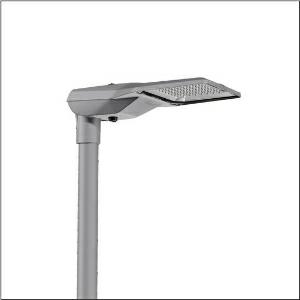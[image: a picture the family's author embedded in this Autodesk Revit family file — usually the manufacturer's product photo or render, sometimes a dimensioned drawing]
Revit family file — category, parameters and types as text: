
# Revit family: streetlight_sl_21_iq_midi___pc-r_5xe3g31y08mb_65a2
name_source: partatom
category: Lighting Fixtures
units: mm (PartAtom-declared; Revit-internal decimal feet)

## family parameters
Cut with Voids When Loaded = No
Host = Face
Light Source = No
Part Type = Normal
Room Calculation Point = No
Round Connector Dimension = Use Diameter
Shared = No

## types (1)
- --- (1 x LED, 17070 lm, 129.3 W, 3000K)
    Apparent Load = 129 VA
    CIE Flux Codes = 38 78 98 100 100
    Color Rendering = 70
    Color Temperature = 3000K
    Default Elevation = 1800 mm
    Description = Streetlight SL 21 iQ midi, mast luminaire, primary light control with lens, of PMMA, primary optical cover: cover, of toughened safety glass, transparent, light distribution: PC-R, light emission: direct distribution, primary light characteristic: asymmetric, right, installation type: post-top, side-entry, LED, High Power LED, rated luminous flux: 17.070lm, luminous efficacy: 132lm/W, light colour: 730, colour temperature: 3000K, control gear: iQ-Street Remote, D4i with power reduction, control: pre-setting: logarithmic dimming characteristic, Street-Remote, Auto-Match, Temp-Guard, Lumen-Switch, Night-Set, Smart-Wire, Light-Fading, Desk-Remote (wireless, voltage-free reading and setting of iQ features in the workshop via application-optimized NFC function/RFID function), optimised constant luminous flux control (CLO 2.0), mains connection: 230..240V, AC, 50/60Hz, start of lifetime: 129W, end of service life: 142W, reduction: 56W, luminaire housing, of diecast aluminium, powder-coated, Siteco® metallic grey (DB 702S), corrosivity category C5 mid according to DIN EN ISO 12944, please order mast flange separately, inclination adjustable: 0°, 5°, 10°, 15°, sealing non-destructively replaceable, multi-level sealing system, length: 644mm, width: 335mm, height: 110mm, mast flange for spigot size: 42mm (side-entry): 5XC10008XM4, 60/48mm (side-entry/post-top): 5XC10108XM2, 76/60mm (side-entry/post-top): 5XC10108XM1, mounting height: 4..8m, Smart Interface below and above, protection rating (complete): IP66, insulation class (complete): insulation class II (safety insulation), certification: CE, ENEC, ENEC+, VDE, impact resistance: IK10, permissible operating ambient temperature for outdoor applications: -40..+50°C, standard-compliant lighting for roads and squares, packaging unit: 1 piece

Light Distribution: PC-R
    Height = 111 mm
    Lamp = 1 x LED
    Lamp Light Flux = 17070 lm
    Lamp Power = 129.3 W
    Lamp count = 1
    Length = 644 mm
    Luminous efficacy = 132 lm/W
    Manufacturer = Siteco
    ModVariant = No
    Model = 5XE3G31Y08MB
    Number of Poles = 1
    OnlyDefault = Yes
    Power Factor = 1
    Product Name = Streetlight SL 21 iQ midi | PC-R
    Product group = mast luminaire | pylon top
    ProductGroupID = 6100
    Protection Class = Protection class II
    Protection Degree = IP 66
    RLX_Detail_Level = 1
    RLX_Emergency_Light_Flux = 0 lm
    RLX_Emergency_Type = 0
    RLX_Emergency_Type_DB = No
    RlxData = <blob elided: 29677 chars, md5=bdcbb309>
    Socket = socket
    Standby Power = 0 W
    System Light Flux = 17070 lm
    System Power = 129 W
    Type Comments = factory setting: luminous flux: 100 % | dim-lin: 254 | 672 mA
    Type Image = l_1004304.jpg
    URL = http://relux.com
    VarID = @adj_085611
    Voltage = 0 V
    Weight = 0.00 kg
    Width = 336 mm

## geometry (parser evidence)
native form markers: Blend x4, Sweep x10
no freeform markers — native parametric forms only
